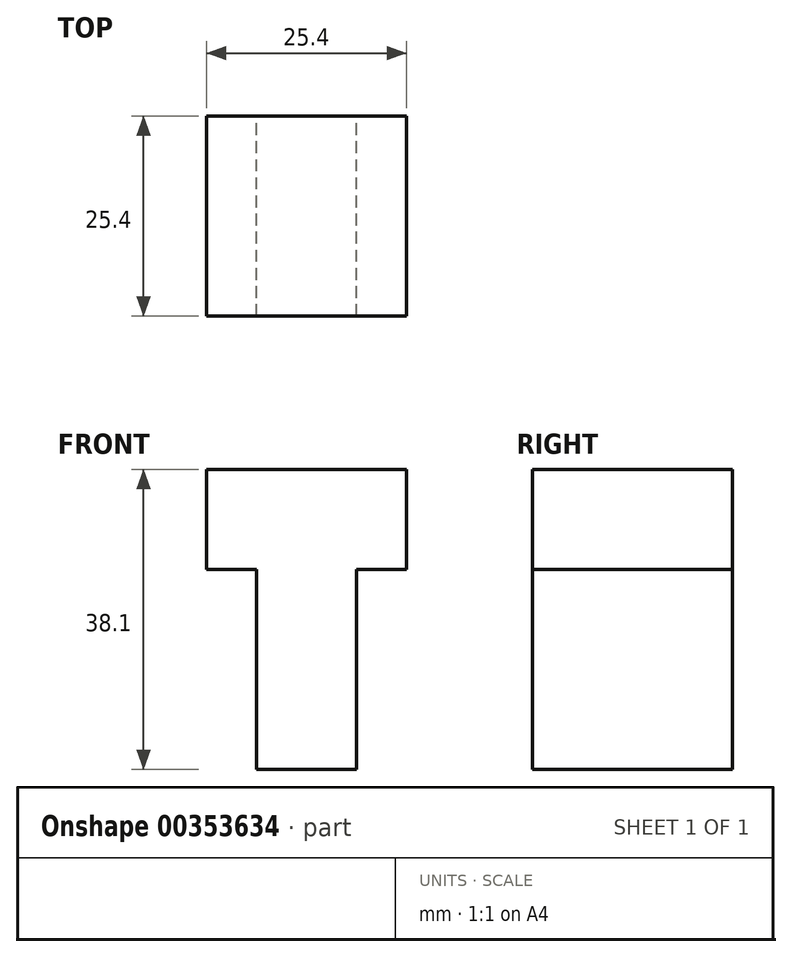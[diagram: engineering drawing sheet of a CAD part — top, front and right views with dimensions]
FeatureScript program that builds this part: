
annotation { "Feature Type Name" : "Feature", "Feature Type Description" : "" }
export const myFeature = defineFeature(function(context is Context, id is Id, definition is map)
    precondition{}
    {
        {
            var Q0;
            Q0=qCreatedBy(makeId("Front.planeOp"),FACE);
            var sketch = newSketch(context, id + "F0", { "sketchPlane" : qUnion([Q0])});
            skLineSegment(sketch, "E0", {"start": v(0, 0) * mm, "end": v(0, 25.4) * mm});
            skLineSegment(sketch, "E1", {"start": v(0, 25.4) * mm, "end": v(-6.35, 25.4) * mm});
            skLineSegment(sketch, "E2", {"start": v(-6.35, 25.4) * mm, "end": v(-6.35, 38.1) * mm});
            skLineSegment(sketch, "E3", {"start": v(12.7, 25.4) * mm, "end": v(12.7, 0) * mm});
            skLineSegment(sketch, "E4", {"start": v(12.7, 0) * mm, "end": v(0, 0) * mm});
            skLineSegment(sketch, "E5", {"start": v(12.7, 25.4) * mm, "end": v(19.05, 25.4) * mm});
            skLineSegment(sketch, "E6", {"start": v(19.05, 25.4) * mm, "end": v(19.05, 38.1) * mm});
            skLineSegment(sketch, "E7", {"start": v(-6.35, 38.1) * mm, "end": v(19.05, 38.1) * mm});
            skSolve(sketch);
        }
        {
            var Q0;
            Q0 = qSketchRegion(id + "F0", true);
            extrude(context, id + "F1", {"entities" : qUnion([Q0]), "depth" : 25.4 * mm});
        }
    });
